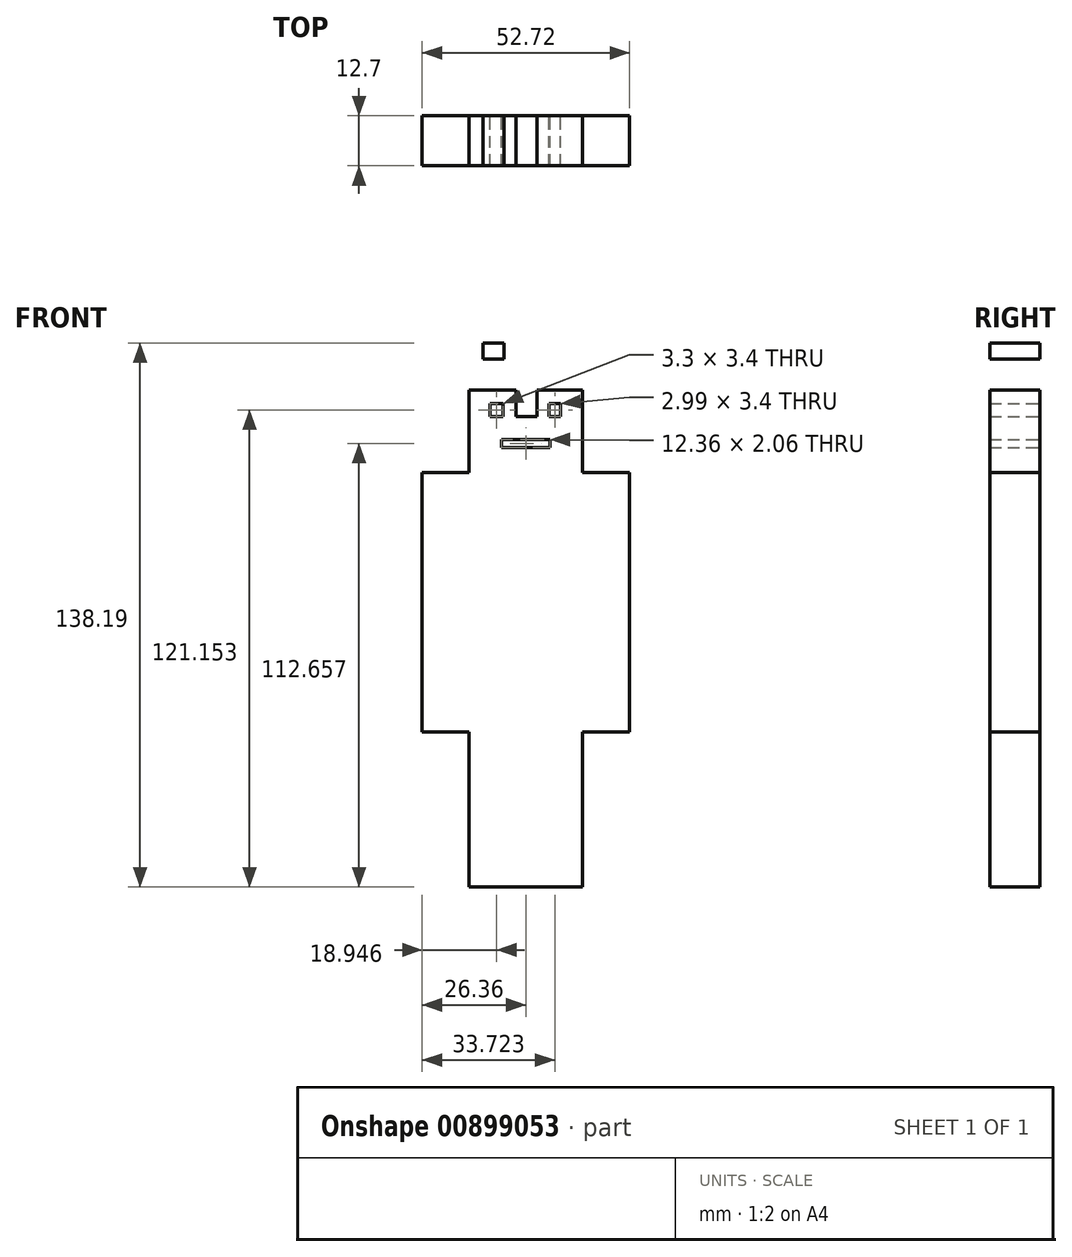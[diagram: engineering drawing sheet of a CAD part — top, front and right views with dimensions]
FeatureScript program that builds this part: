
annotation { "Feature Type Name" : "Feature", "Feature Type Description" : "" }
export const myFeature = defineFeature(function(context is Context, id is Id, definition is map)
    precondition{}
    {
        {
            var Q0;
            Q0=qCreatedBy(makeId("Front.planeOp"),FACE);
            var sketch = newSketch(context, id + "F0", { "sketchPlane" : qUnion([Q0])});
            skLineSegment(sketch, "E0.bottom", {"start": v(-14.42, 35.46) * mm, "end": v(14.35, 35.46) * mm});
            skLineSegment(sketch, "E0.left", {"start": v(-14.42, 35.46) * mm, "end": v(-14.42, 56.43) * mm});
            skLineSegment(sketch, "E0.right", {"start": v(14.35, 35.46) * mm, "end": v(14.35, 56.42) * mm});
            skPoint(sketch, "E1.middle", {"position": v(-14.42, 35.46) * mm});
            skLineSegment(sketch, "E2.bottom", {"start": v(-14.42, 35.46) * mm, "end": v(-26.36, 35.46) * mm});
            skLineSegment(sketch, "E2.top", {"start": v(-14.42, -30.48) * mm, "end": v(-26.36, -30.48) * mm});
            skLineSegment(sketch, "E2.left", {"start": v(-14.42, 35.46) * mm, "end": v(-14.42, -30.48) * mm});
            skLineSegment(sketch, "E2.right", {"start": v(-26.36, 35.46) * mm, "end": v(-26.36, -30.48) * mm});
            skLineSegment(sketch, "E3.bottom", {"start": v(14.35, 35.46) * mm, "end": v(26.36, 35.46) * mm});
            skLineSegment(sketch, "E3.top", {"start": v(14.35, -30.48) * mm, "end": v(26.36, -30.48) * mm});
            skLineSegment(sketch, "E3.left", {"start": v(14.35, 35.46) * mm, "end": v(14.35, -30.48) * mm});
            skLineSegment(sketch, "E3.right", {"start": v(26.36, 35.46) * mm, "end": v(26.36, -30.48) * mm});
            skLineSegment(sketch, "E4", {"start": v(-14.42, -30.48) * mm, "end": v(14.35, -30.48) * mm});
            skLineSegment(sketch, "E5.bottom", {"start": v(-14.42, -30.48) * mm, "end": v(0, -30.48) * mm});
            skLineSegment(sketch, "E5.top", {"start": v(-14.42, -69.82) * mm, "end": v(0, -69.82) * mm});
            skLineSegment(sketch, "E5.left", {"start": v(-14.42, -30.48) * mm, "end": v(-14.42, -69.82) * mm});
            skLineSegment(sketch, "E5.right", {"start": v(0, -30.48) * mm, "end": v(0, -69.82) * mm});
            skLineSegment(sketch, "E6.bottom", {"start": v(14.35, -30.48) * mm, "end": v(0, -30.48) * mm});
            skLineSegment(sketch, "E6.top", {"start": v(14.35, -69.82) * mm, "end": v(0, -69.82) * mm});
            skLineSegment(sketch, "E6.left", {"start": v(14.35, -30.48) * mm, "end": v(14.35, -69.82) * mm});
            skLineSegment(sketch, "E7.left", {"start": v(0, -45.72) * mm, "end": v(0, -39.34) * mm});
            skLineSegment(sketch, "E8", {"start": v(-26.36, 21.42) * mm, "end": v(-14.42, 21.42) * mm});
            skLineSegment(sketch, "E9", {"start": v(14.35, 21.42) * mm, "end": v(26.36, 21.42) * mm});
            skLineSegment(sketch, "E10", {"start": v(-14.42, 56.43) * mm, "end": v(-2.47, 56.43) * mm});
            skLineSegment(sketch, "E11", {"start": v(-2.47, 56.43) * mm, "end": v(-2.47, 49.63) * mm});
            skLineSegment(sketch, "E12", {"start": v(-2.47, 49.63) * mm, "end": v(2.88, 49.63) * mm});
            skLineSegment(sketch, "E13", {"start": v(2.88, 49.63) * mm, "end": v(2.88, 56.42) * mm});
            skLineSegment(sketch, "E14", {"start": v(2.88, 56.42) * mm, "end": v(14.35, 56.42) * mm});
            skLineSegment(sketch, "E15", {"start": v(-14.42, 56.84) * mm, "end": v(-14.42, 67.55) * mm});
            skLineSegment(sketch, "E16", {"start": v(-14.42, 67.55) * mm, "end": v(-12.36, 70.02) * mm});
            skLineSegment(sketch, "E17", {"start": v(-12.36, 70.02) * mm, "end": v(10.7, 70.02) * mm});
            skLineSegment(sketch, "E18", {"start": v(10.7, 70.02) * mm, "end": v(14, 67.55) * mm});
            skLineSegment(sketch, "E19", {"start": v(14, 67.55) * mm, "end": v(14.35, 56.42) * mm});
            skLineSegment(sketch, "E20.bottom", {"start": v(-2.47, 53.03) * mm, "end": v(-9.06, 53.03) * mm});
            skLineSegment(sketch, "E20.top", {"start": v(-2.47, 49.63) * mm, "end": v(-9.06, 49.63) * mm});
            skLineSegment(sketch, "E20.left", {"start": v(-2.47, 53.03) * mm, "end": v(-2.47, 49.63) * mm});
            skLineSegment(sketch, "E20.right", {"start": v(-9.06, 53.03) * mm, "end": v(-9.06, 49.63) * mm});
            skLineSegment(sketch, "E21", {"start": v(-5.77, 53.03) * mm, "end": v(-5.77, 49.63) * mm});
            skLineSegment(sketch, "E22.bottom", {"start": v(2.88, 53.03) * mm, "end": v(8.86, 53.03) * mm});
            skLineSegment(sketch, "E22.top", {"start": v(2.88, 49.63) * mm, "end": v(8.86, 49.63) * mm});
            skLineSegment(sketch, "E22.left", {"start": v(2.88, 53.03) * mm, "end": v(2.88, 49.63) * mm});
            skLineSegment(sketch, "E22.right", {"start": v(8.86, 53.03) * mm, "end": v(8.86, 49.63) * mm});
            skLineSegment(sketch, "E23", {"start": v(5.87, 53.03) * mm, "end": v(5.87, 49.63) * mm});
            skLineSegment(sketch, "E24.bottom", {"start": v(-6.18, 43.87) * mm, "end": v(6.18, 43.87) * mm});
            skLineSegment(sketch, "E24.top", {"start": v(-6.18, 41.8) * mm, "end": v(6.18, 41.8) * mm});
            skLineSegment(sketch, "E24.left", {"start": v(-6.18, 43.87) * mm, "end": v(-6.18, 41.8) * mm});
            skLineSegment(sketch, "E24.right", {"start": v(6.18, 43.87) * mm, "end": v(6.18, 41.8) * mm});
            skLineSegment(sketch, "E25", {"start": v(2.88, 53.03) * mm, "end": v(5.87, 53.03) * mm});
            skLineSegment(sketch, "E26", {"start": v(2.88, 53.03) * mm, "end": v(5.25, 53.03) * mm});
            skLineSegment(sketch, "E27", {"start": v(5.25, 53.03) * mm, "end": v(2.88, 53.03) * mm});
            skLineSegment(sketch, "E28", {"start": v(2.88, 53.03) * mm, "end": v(4.38, 53.03) * mm});
            skLineSegment(sketch, "E29", {"start": v(-14.42, -60.34) * mm, "end": v(0, -60.34) * mm});
            skLineSegment(sketch, "E30", {"start": v(0, -60.34) * mm, "end": v(14.35, -60.34) * mm});
            skLineSegment(sketch, "E31.bottom", {"start": v(-10.92, 64.26) * mm, "end": v(-5.56, 64.26) * mm});
            skLineSegment(sketch, "E31.top", {"start": v(-10.92, 68.37) * mm, "end": v(-5.56, 68.37) * mm});
            skLineSegment(sketch, "E31.left", {"start": v(-10.92, 64.26) * mm, "end": v(-10.92, 68.37) * mm});
            skLineSegment(sketch, "E31.right", {"start": v(-5.56, 64.26) * mm, "end": v(-5.56, 68.37) * mm});
            skPoint(sketch, "E31.middle", {"position": v(-8.24, 66.31) * mm});
            skLineSegment(sketch, "E32", {"start": v(-11.74, -64.87) * mm, "end": v(-3.5, -64.87) * mm});
            skLineSegment(sketch, "E33", {"start": v(3.7, -64.26) * mm, "end": v(10.7, -64.26) * mm});
            skLineSegment(sketch, "E34", {"start": v(-44.48, 72.29) * mm, "end": v(-44.48, -70.64) * mm});
            skLineSegment(sketch, "E35", {"start": v(-44.48, 72.29) * mm, "end": v(42.84, 72.29) * mm});
            skLineSegment(sketch, "E36", {"start": v(-42.84, -70.64) * mm, "end": v(43.25, -70.43) * mm});
            skLineSegment(sketch, "E37", {"start": v(42.84, 72.29) * mm, "end": v(42.84, -70.43) * mm});
            skSolve(sketch);
        }
        {
            var Q0;
            Q0 = qSketchRegion(id + "F0", true);
            extrude(context, id + "F1", {"entities" : qUnion([Q0]), "depth" : 12.7 * mm, "offsetDistance" : 25.4 * mm});
        }
    });
